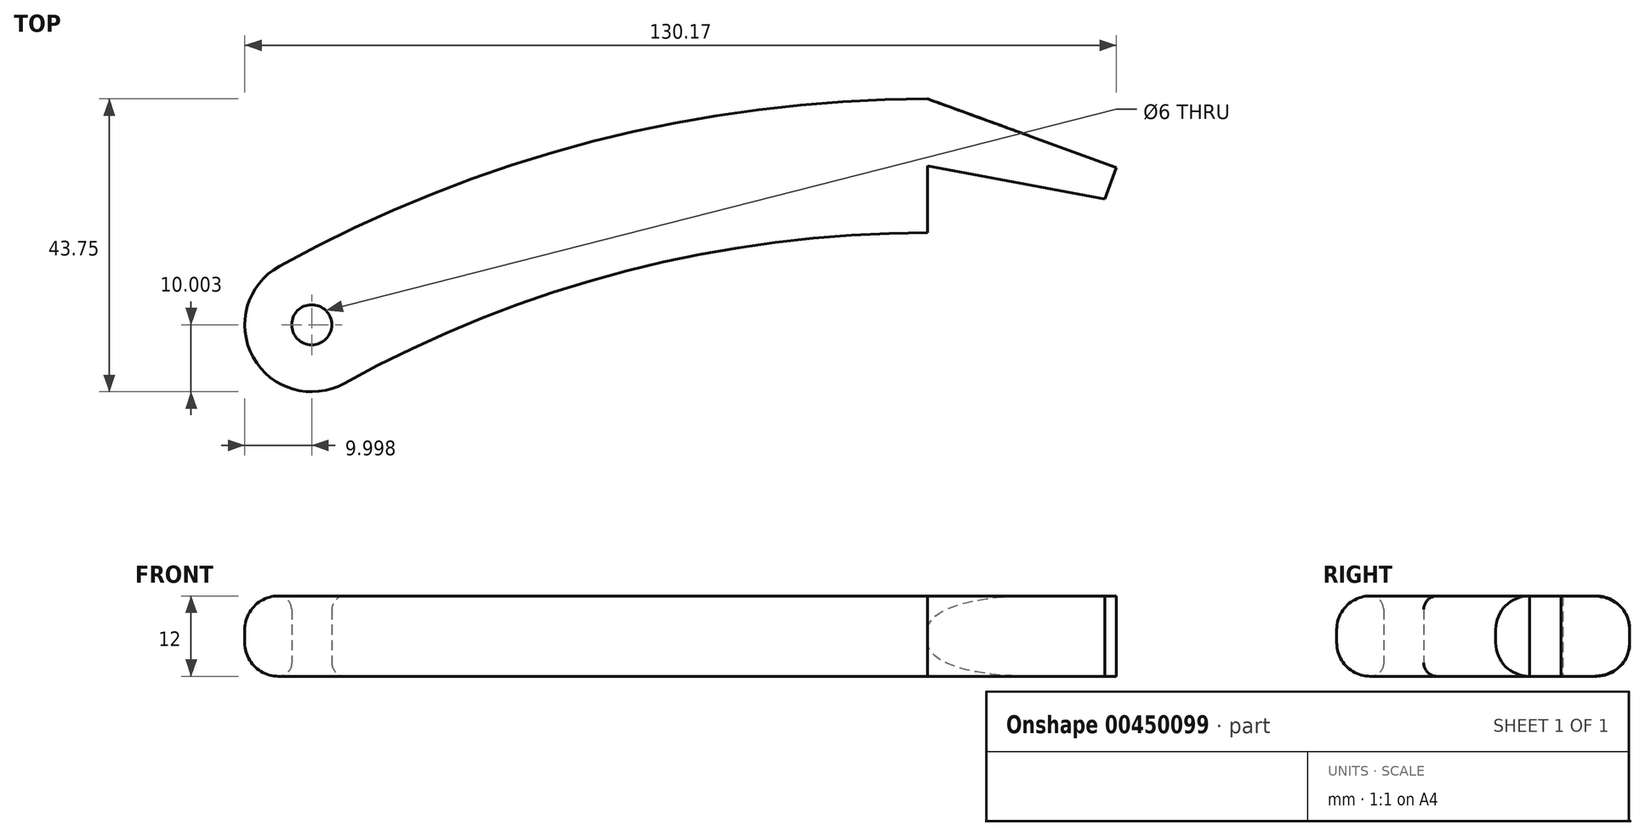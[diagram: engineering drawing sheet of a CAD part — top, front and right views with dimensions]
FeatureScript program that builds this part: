
annotation { "Feature Type Name" : "Feature", "Feature Type Description" : "" }
export const myFeature = defineFeature(function(context is Context, id is Id, definition is map)
    precondition{}
    {
        {
            var Q0;
            Q0=qCreatedBy(makeId("Top.planeOp"),FACE);
            var sketch = newSketch(context, id + "F0", { "sketchPlane" : qUnion([Q0])});
            skArc(sketch, "E0", {"start": v(12.5, 177.73) * mm, "mid": v(-37.5, 171.38) * mm, "end": v(-84.33, 152.73) * mm});
            skArc(sketch, "E1", {"start": v(12.5, 157.73) * mm, "mid": v(-32.5, 152.02) * mm, "end": v(-74.65, 135.23) * mm});
            skArc(sketch, "E2", {"start": v(-84.33, 152.73) * mm, "mid": v(-88.24, 139.14) * mm, "end": v(-74.65, 135.23) * mm});
            skLineSegment(sketch, "E3", {"start": v(12.5, 177.73) * mm, "end": v(40.68, 167.47) * mm});
            skLineSegment(sketch, "E4", {"start": v(40.68, 167.47) * mm, "end": v(38.97, 162.77) * mm});
            skLineSegment(sketch, "E5", {"start": v(38.97, 162.77) * mm, "end": v(12.5, 167.73) * mm});
            skLineSegment(sketch, "E6", {"start": v(12.5, 167.73) * mm, "end": v(12.5, 157.73) * mm});
            skLineSegment(sketch, "E7", {"start": v(12.5, 177.73) * mm, "end": v(12.5, 208.98) * mm, "construction": true});
            skCircle(sketch, "E8", {"center": v(-79.5, 143.98) * mm, "radius": 3 * mm});
            skSolve(sketch);
        }
        {
            var Q0;
            Q0 = qSketchRegion(id + "F0", true);
            extrude(context, id + "F1", {"entities" : qUnion([Q0]), "depth" : 12 * mm});
        }
        {
            var Q0;
            Q0=makeQuery(id+"F1.opExtrude","CAP_EDGE",EDGE,{"disambiguationData":[OSD([sQuery(id+"F0.wireOp",EDGE,"E1")])],"isStart":false});
            var Q1;
            Q1=makeQuery(id+"F1.opExtrude","CAP_EDGE",EDGE,{"disambiguationData":[OSD([sQuery(id+"F0.wireOp",EDGE,"E1")])],"isStart":true});
            fillet(context, id + "F2", {"entities" : qUnion([Q0, Q1]), "radius" : 5 * mm, "tangentPropagation" : true, "allowEdgeOverflow" : false});
        }
        {
            var Q0;
            Q0=makeQuery(id+"F1.opExtrude","CAP_EDGE",EDGE,{"disambiguationData":[OSD([sQuery(id+"F0.wireOp",EDGE,"E8")])],"isStart":false});
            var Q1;
            Q1=makeQuery(id+"F1.opExtrude","CAP_EDGE",EDGE,{"disambiguationData":[OSD([sQuery(id+"F0.wireOp",EDGE,"E8")])],"isStart":true});
            fillet(context, id + "F3", {"entities" : qUnion([Q0, Q1]), "radius" : 2 * mm, "tangentPropagation" : true, "allowEdgeOverflow" : false});
        }
    });
